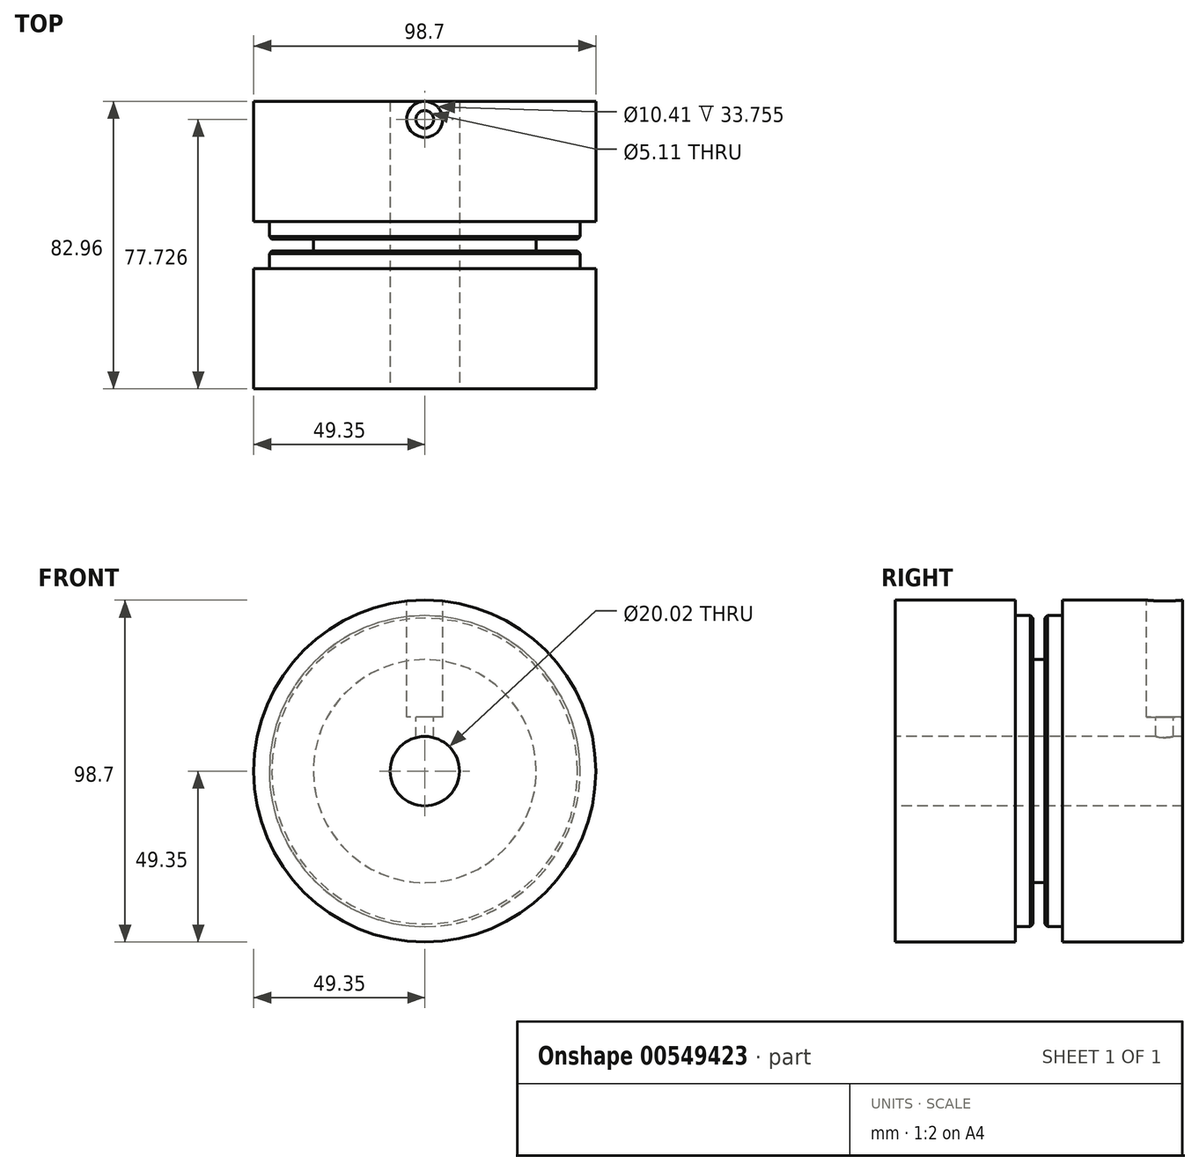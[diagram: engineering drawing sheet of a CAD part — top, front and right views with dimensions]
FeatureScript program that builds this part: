
annotation { "Feature Type Name" : "Feature", "Feature Type Description" : "" }
export const myFeature = defineFeature(function(context is Context, id is Id, definition is map)
    precondition{}
    {
        {
            var Q0;
            Q0=qCreatedBy(makeId("Right.planeOp"),FACE);
            var sketch = newSketch(context, id + "F0", { "sketchPlane" : qUnion([Q0])});
            skLineSegment(sketch, "E0", {"start": v(-35.21, 0) * mm, "end": v(33.24, 0) * mm, "construction": true});
            skLineSegment(sketch, "E1", {"start": v(0, 10) * mm, "end": v(-41.48, 10) * mm});
            skLineSegment(sketch, "E2", {"start": v(-41.48, 10) * mm, "end": v(-41.48, 49.35) * mm});
            skLineSegment(sketch, "E3", {"start": v(-41.48, 49.35) * mm, "end": v(-6.8, 49.35) * mm});
            skLineSegment(sketch, "E4", {"start": v(-6.8, 49.35) * mm, "end": v(-6.8, 44.88) * mm});
            skLineSegment(sketch, "E5", {"start": v(-6.8, 44.88) * mm, "end": v(-1.71, 44.88) * mm});
            skLineSegment(sketch, "E6", {"start": v(0, 44.88) * mm, "end": v(0, 10) * mm, "construction": true});
            skLineSegment(sketch, "E7.MirrorCS", {"start": v(6.8, 44.88) * mm, "end": v(1.71, 44.88) * mm});
            skLineSegment(sketch, "E8.MirrorCS", {"start": v(6.8, 49.35) * mm, "end": v(6.8, 44.88) * mm});
            skLineSegment(sketch, "E9.MirrorCS", {"start": v(41.48, 49.35) * mm, "end": v(6.8, 49.35) * mm});
            skLineSegment(sketch, "E10.MirrorCS", {"start": v(41.48, 10) * mm, "end": v(41.48, 49.35) * mm});
            skLineSegment(sketch, "E11.MirrorCS", {"start": v(0, 10) * mm, "end": v(41.48, 10) * mm});
            skLineSegment(sketch, "E12", {"start": v(-1.71, 44.88) * mm, "end": v(-1.71, 32.18) * mm});
            skLineSegment(sketch, "E13", {"start": v(-1.71, 32.18) * mm, "end": v(1.71, 32.18) * mm});
            skLineSegment(sketch, "E14", {"start": v(1.71, 32.18) * mm, "end": v(1.71, 44.88) * mm});
            skPoint(sketch, "E15.orphan", {"position": v(0, 44.88) * mm});
            skSolve(sketch);
        }
        {
            var Q0;
            Q0=qSketchRegion(id+"F0",true);
            var Q1;
            Q1=sQuery(id+"F0.wireOp",EDGE,"E0");
            revolve(context, id + "F1", {"entities" : qUnion([Q0]), "axis" : qUnion([Q1]), "revolveType" : RevolveType.FULL});
        }
        {
            var Q0;
            Q0=makeQuery(id+"F1.opRevolve","SWEPT_EDGE",EDGE,{"disambiguationData":[OSD([sQuery(id+"F0.wireOp",EDGE,"E7.MirrorCS"),sQuery(id+"F0.wireOp",EDGE,"E14")])]});
            var Q1;
            Q1=makeQuery(id+"F1.opRevolve","SWEPT_EDGE",EDGE,{"disambiguationData":[OSD([sQuery(id+"F0.wireOp",EDGE,"E5"),sQuery(id+"F0.wireOp",EDGE,"E12")])]});
            chamfer(context, id + "F2", {"entities" : qUnion([Q0, Q1]), "width" : 0.76 * mm, "tangentPropagation" : true});
        }
        {
            var Q0;
            Q0=makeQuery(id+"F1.opRevolve","SWEPT_EDGE",EDGE,{"disambiguationData":[OSD([sQuery(id+"F0.wireOp",EDGE,"E12"),sQuery(id+"F0.wireOp",EDGE,"E13")])]});
            var Q1;
            Q1=makeQuery(id+"F1.opRevolve","SWEPT_EDGE",EDGE,{"disambiguationData":[OSD([sQuery(id+"F0.wireOp",EDGE,"E13"),sQuery(id+"F0.wireOp",EDGE,"E14")])]});
            fillet(context, id + "F3", {"entities" : qUnion([Q0, Q1]), "radius" : 0.25 * mm, "tangentPropagation" : true, "allowEdgeOverflow" : false});
        }
        {
            var Q0;
            Q0=qCreatedBy(makeId("Top.planeOp"),FACE);
            cPlane(context, id + "F4", {"entities" : qUnion([Q0]), "cplaneType" : CPlaneType.OFFSET, "offset" : 49.35 * mm, "width" : 152.4 * mm, "height" : 152.4 * mm});
        }
        {
            var Q0;
            Q0=qCreatedBy(id+"F4.planeOp",FACE);
            var sketch = newSketch(context, id + "F5", { "sketchPlane" : qUnion([Q0])});
            skPoint(sketch, "E16", {"position": v(0, 36.25) * mm});
            skLineSegment(sketch, "E17.0", {"start": v(49.35, 41.48) * mm, "end": v(-49.35, 41.48) * mm});
            skCircle(sketch, "E18", {"center": v(0, 36.25) * mm, "radius": 5.23 * mm, "construction": true});
            skSolve(sketch);
        }
        {
            var Q0;
            Q0=sQuery(id+"F5.wireOp",VERTEX,"E16");
            var Q1;
            Q1=makeQuery(id+"F1.opRevolve","SWEPT_BODY",BODY,{"disambiguationData":[OSD([sQuery(id+"F0.wireOp",EDGE,"E1"),sQuery(id+"F0.wireOp",EDGE,"E2"),sQuery(id+"F0.wireOp",EDGE,"E3"),sQuery(id+"F0.wireOp",EDGE,"E4"),sQuery(id+"F0.wireOp",EDGE,"E5"),sQuery(id+"F0.wireOp",EDGE,"E7.MirrorCS"),sQuery(id+"F0.wireOp",EDGE,"E8.MirrorCS"),sQuery(id+"F0.wireOp",EDGE,"E9.MirrorCS"),sQuery(id+"F0.wireOp",EDGE,"E10.MirrorCS"),sQuery(id+"F0.wireOp",EDGE,"E11.MirrorCS"),sQuery(id+"F0.wireOp",EDGE,"E12"),sQuery(id+"F0.wireOp",EDGE,"E13"),sQuery(id+"F0.wireOp",EDGE,"E14")])]});
            hole(context, id + "F6", {"style" : HoleStyle.C_BORE, "endStyle" : HoleEndStyle.BLIND, "holeDiameter" : 5.1 * mm, "cBoreDiameter" : 10.4 * mm, "cBoreDepth" : 33.48 * mm, "holeDepth" : 49.35 * mm, "isTappedThrough" : true, "tappedDepth" : 12.7 * mm, "tapClearance" : 3, "locations" : qUnion([Q0]), "scope" : qUnion([Q1])});
        }
    });
